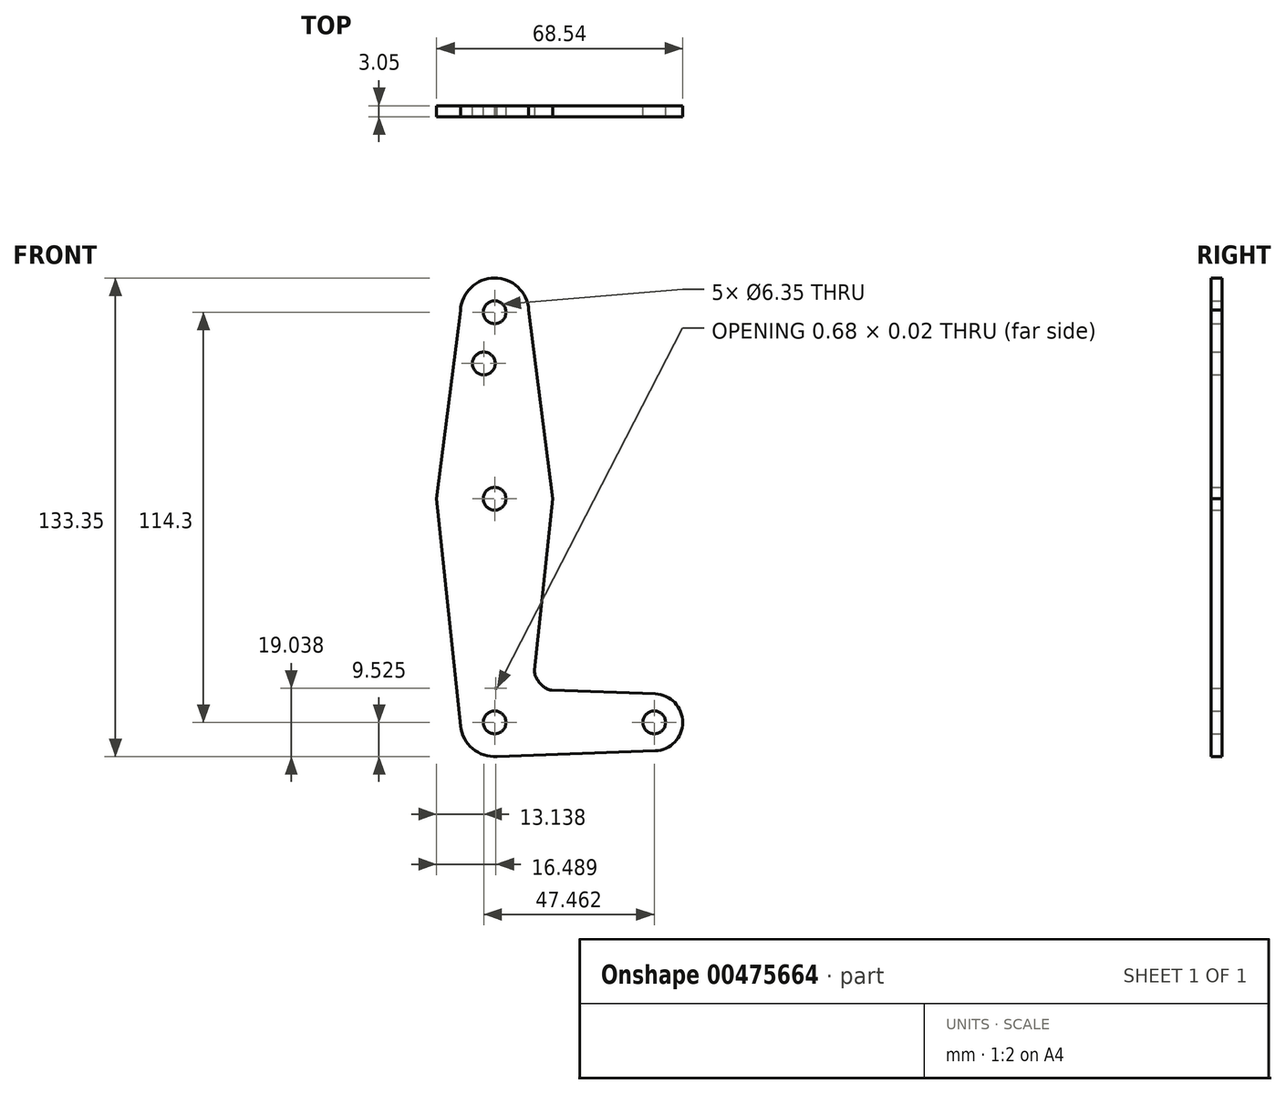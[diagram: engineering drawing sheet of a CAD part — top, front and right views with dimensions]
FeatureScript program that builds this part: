
annotation { "Feature Type Name" : "Feature", "Feature Type Description" : "" }
export const myFeature = defineFeature(function(context is Context, id is Id, definition is map)
    precondition{}
    {
        {
            var Q0;
            Q0=qCreatedBy(makeId("Front.planeOp"),FACE);
            var sketch = newSketch(context, id + "F0", { "sketchPlane" : qUnion([Q0])});
            skLineSegment(sketch, "E0", {"start": v(0, 51.98) * mm, "end": v(0, -62.32) * mm});
            skLineSegment(sketch, "E1", {"start": v(0, -62.32) * mm, "end": v(44.45, -62.32) * mm});
            skCircle(sketch, "E2", {"center": v(0, 51.98) * mm, "radius": 9.53 * mm});
            skCircle(sketch, "E3", {"center": v(0, 1.18) * mm, "radius": 15.88 * mm});
            skCircle(sketch, "E4", {"center": v(0, -62.32) * mm, "radius": 9.53 * mm});
            skCircle(sketch, "E5", {"center": v(44.45, -62.32) * mm, "radius": 7.94 * mm});
            skLineSegment(sketch, "E6", {"start": v(-9.51, 52.5) * mm, "end": v(-16.15, 0) * mm});
            skLineSegment(sketch, "E7", {"start": v(-16.15, 0) * mm, "end": v(-9.47, -63.32) * mm});
            skLineSegment(sketch, "E8", {"start": v(9.36, 53.72) * mm, "end": v(16.15, 0) * mm});
            skLineSegment(sketch, "E9", {"start": v(16.15, 0) * mm, "end": v(9.58, -62.32) * mm});
            skLineSegment(sketch, "E10", {"start": v(0, -71.85) * mm, "end": v(44.73, -70.26) * mm});
            skCircle(sketch, "E11", {"center": v(0, 51.98) * mm, "radius": 3.18 * mm});
            skCircle(sketch, "E12", {"center": v(0, 0) * mm, "radius": 3.18 * mm});
            skCircle(sketch, "E13", {"center": v(0, -62.32) * mm, "radius": 3.18 * mm});
            skCircle(sketch, "E14", {"center": v(44.45, -62.32) * mm, "radius": 3.18 * mm});
            skLineSegment(sketch, "E15", {"start": v(0, -52.8) * mm, "end": v(44.73, -54.4) * mm});
            skCircle(sketch, "E16", {"center": v(-3.01, 37.7) * mm, "radius": 3.18 * mm});
            skPoint(sketch, "E16.first.point", {"position": v(0, 36.7) * mm});
            skPoint(sketch, "E16.second.point", {"position": v(-6.17, 37.37) * mm});
            skPoint(sketch, "E16.third.point", {"position": v(-2.03, 40.72) * mm});
            skSolve(sketch);
        }
        {
            var Q0;
            Q0 = qSketchRegion(id + "F0", true);
            var Q1;
            {var subQ0=sQuery(id+"F0.wireOp",EDGE,"E13");var subQ3=sQuery(id+"F0.wireOp",EDGE,"E1");var subQ4=makeQuery(id+"F0.imprint","INTERSECT",VERTEX,{"derivedFrom":[subQ3,subQ0]});Q1=makeQuery(id+"F0.imprint","IMPRINT",FACE,{"disambiguationData":[TD([[makeQuery(id+"F0.imprint","IMPRINT",EDGE,{"disambiguationData":[TD([[subQ4,-1.0]])],"derivedFrom":subQ3}),1.0]])]});}
            extrude(context, id + "F1", {"entities" : qUnion([Q0, Q1]), "depth" : 3.05 * mm});
        }
        {
            var Q0;
            Q0=makeQuery(id+"F1.opExtrude","SWEPT_EDGE",EDGE,{"disambiguationData":[OSD([sQuery(id+"F0.wireOp",EDGE,"E9"),sQuery(id+"F0.wireOp",EDGE,"E15")])]});
            fillet(context, id + "F2", {"entities" : qUnion([Q0]), "radius" : 5.08 * mm, "tangentPropagation" : true, "rho" : .313, "crossSection" : FilletCrossSection.CONIC, "allowEdgeOverflow" : false});
        }
    });
